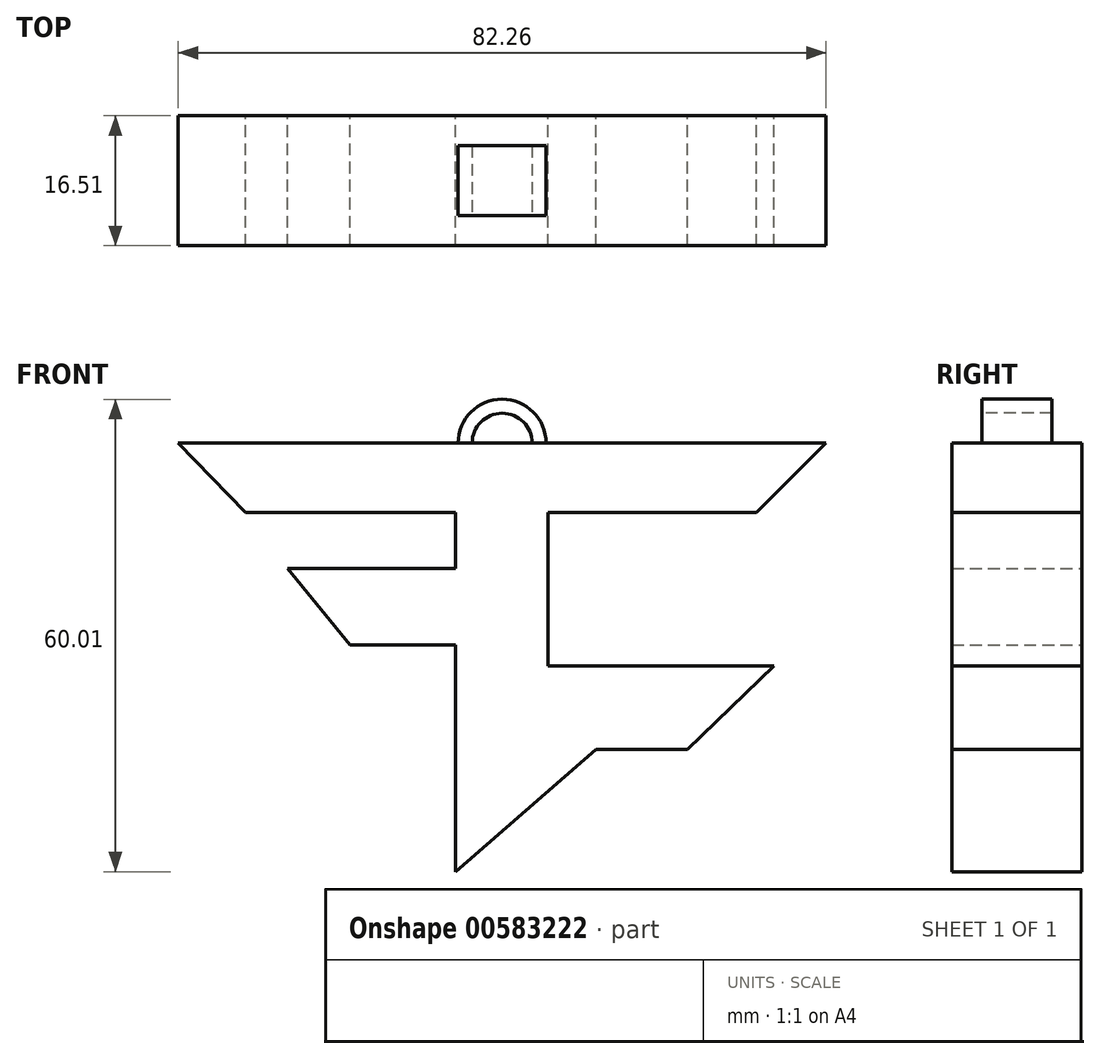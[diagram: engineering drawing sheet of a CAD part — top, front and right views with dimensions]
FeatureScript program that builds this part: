
annotation { "Feature Type Name" : "Feature", "Feature Type Description" : "" }
export const myFeature = defineFeature(function(context is Context, id is Id, definition is map)
    precondition{}
    {
        {
            var Q0;
            Q0=qCreatedBy(makeId("Front.planeOp"),FACE);
            var sketch = newSketch(context, id + "F0", { "sketchPlane" : qUnion([Q0])});
            skLineSegment(sketch, "E0", {"start": v(-131.37, 102.72) * mm, "end": v(-49.1, 102.72) * mm});
            skLineSegment(sketch, "E1", {"start": v(-49.1, 102.72) * mm, "end": v(-57.96, 93.95) * mm});
            skLineSegment(sketch, "E2", {"start": v(-57.96, 93.95) * mm, "end": v(-84.39, 93.95) * mm});
            skLineSegment(sketch, "E3", {"start": v(-84.39, 93.95) * mm, "end": v(-84.39, 74.4) * mm});
            skLineSegment(sketch, "E4", {"start": v(-84.39, 74.4) * mm, "end": v(-55.7, 74.4) * mm});
            skLineSegment(sketch, "E5", {"start": v(-55.7, 74.4) * mm, "end": v(-66.72, 63.82) * mm});
            skLineSegment(sketch, "E6", {"start": v(-66.72, 63.82) * mm, "end": v(-78.31, 63.82) * mm});
            skLineSegment(sketch, "E7", {"start": v(-78.31, 63.82) * mm, "end": v(-96.14, 48.29) * mm});
            skLineSegment(sketch, "E8", {"start": v(-96.14, 48.29) * mm, "end": v(-96.14, 77.09) * mm});
            skLineSegment(sketch, "E9", {"start": v(-96.14, 77.09) * mm, "end": v(-109.57, 77.09) * mm});
            skLineSegment(sketch, "E10", {"start": v(-109.57, 77.09) * mm, "end": v(-117.51, 86.78) * mm});
            skLineSegment(sketch, "E11", {"start": v(-117.51, 86.78) * mm, "end": v(-96.14, 86.78) * mm});
            skLineSegment(sketch, "E12", {"start": v(-96.14, 86.78) * mm, "end": v(-96.14, 93.95) * mm});
            skLineSegment(sketch, "E13", {"start": v(-96.14, 93.95) * mm, "end": v(-122.84, 93.95) * mm});
            skLineSegment(sketch, "E14", {"start": v(-122.84, 93.95) * mm, "end": v(-131.37, 102.72) * mm});
            skSolve(sketch);
        }
        {
            var Q0;
            Q0=makeQuery(id+"F0.imprint","IMPRINT",FACE,{"disambiguationData":[TD([[makeQuery(id+"F0.imprint","IMPRINT",EDGE,{"derivedFrom":sQuery(id+"F0.wireOp",EDGE,"E0")}),-1.0]])]});
            extrude(context, id + "F1", {"entities" : qUnion([Q0]), "depth" : 16.5 * mm, "offsetDistance" : 25.4 * mm});
        }
        {
            var Q0;
            Q0=makeQuery(id+"F1.opExtrude","CAP_FACE",FACE,{"disambiguationData":[OSD([sQuery(id+"F0.wireOp",EDGE,"E0"),sQuery(id+"F0.wireOp",EDGE,"E1"),sQuery(id+"F0.wireOp",EDGE,"E2"),sQuery(id+"F0.wireOp",EDGE,"E3"),sQuery(id+"F0.wireOp",EDGE,"E4"),sQuery(id+"F0.wireOp",EDGE,"E5"),sQuery(id+"F0.wireOp",EDGE,"E6"),sQuery(id+"F0.wireOp",EDGE,"E7"),sQuery(id+"F0.wireOp",EDGE,"E8"),sQuery(id+"F0.wireOp",EDGE,"E9"),sQuery(id+"F0.wireOp",EDGE,"E10"),sQuery(id+"F0.wireOp",EDGE,"E11"),sQuery(id+"F0.wireOp",EDGE,"E12"),sQuery(id+"F0.wireOp",EDGE,"E13"),sQuery(id+"F0.wireOp",EDGE,"E14")])],"isStart":false});
            var sketch = newSketch(context, id + "F2", { "sketchPlane" : qUnion([Q0])});
            skArc(sketch, "E15", {"start": v(-86.43, 102.72) * mm, "mid": v(-90.24, 106.53) * mm, "end": v(-94.05, 102.72) * mm});
            skArc(sketch, "E16", {"start": v(-84.65, 102.72) * mm, "mid": v(-90.24, 108.3) * mm, "end": v(-95.83, 102.72) * mm});
            skSolve(sketch);
        }
        {
            var Q0;
            {var subQ0=sQuery(id+"F2.wireOp",EDGE,"E15");Q0=makeQuery(id+"F2.imprint","IMPRINT",FACE,{"disambiguationData":[TD([[makeQuery(id+"F2.imprint","IMPRINT",EDGE,{"derivedFrom":subQ0}),-1.0]])]});}
            extrude(context, id + "F3", {"entities" : qUnion([Q0]), "operationType" : NewBodyOperationType.ADD, "oppositeDirection" : true, "depth" : 12.7 * mm, "offsetDistance" : 25.4 * mm});
        }
        {
            var Q0;
            {var subQ0=sQuery(id+"F0.wireOp",EDGE,"E0");Q0=makeQuery(id+"F3.boolean.opBoolean","MERGE",FACE,{"derivedFrom":[makeQuery(id+"F1.opExtrude","CAP_FACE",FACE,{"disambiguationData":[OSD([subQ0,sQuery(id+"F0.wireOp",EDGE,"E1"),sQuery(id+"F0.wireOp",EDGE,"E2"),sQuery(id+"F0.wireOp",EDGE,"E3"),sQuery(id+"F0.wireOp",EDGE,"E4"),sQuery(id+"F0.wireOp",EDGE,"E5"),sQuery(id+"F0.wireOp",EDGE,"E6"),sQuery(id+"F0.wireOp",EDGE,"E7"),sQuery(id+"F0.wireOp",EDGE,"E8"),sQuery(id+"F0.wireOp",EDGE,"E9"),sQuery(id+"F0.wireOp",EDGE,"E10"),sQuery(id+"F0.wireOp",EDGE,"E11"),sQuery(id+"F0.wireOp",EDGE,"E12"),sQuery(id+"F0.wireOp",EDGE,"E13"),sQuery(id+"F0.wireOp",EDGE,"E14")])],"isStart":false}),makeQuery(id+"F3.opExtrude","CAP_FACE",FACE,{"disambiguationData":[OSD([subQ0,sQuery(id+"F2.wireOp",EDGE,"E15"),sQuery(id+"F2.wireOp",EDGE,"E16")])],"isStart":true})]});}
            var sketch = newSketch(context, id + "F4", { "sketchPlane" : qUnion([Q0])});
            skArc(sketch, "E17", {"start": v(-84.65, 102.72) * mm, "mid": v(-90.24, 108.3) * mm, "end": v(-95.83, 102.72) * mm});
            skArc(sketch, "E18", {"start": v(-86.43, 102.72) * mm, "mid": v(-90.24, 106.53) * mm, "end": v(-94.05, 102.72) * mm});
            skLineSegment(sketch, "E19", {"start": v(-95.83, 102.72) * mm, "end": v(-94.05, 102.72) * mm});
            skLineSegment(sketch, "E20", {"start": v(-86.43, 102.72) * mm, "end": v(-84.65, 102.72) * mm});
            skSolve(sketch);
        }
        {
            var Q0;
            Q0=makeQuery(id+"F4.imprint","IMPRINT",FACE,{"disambiguationData":[TD([[makeQuery(id+"F4.imprint","IMPRINT",EDGE,{"derivedFrom":sQuery(id+"F4.wireOp",EDGE,"E17")}),1.0]])]});
            extrude(context, id + "F5", {"entities" : qUnion([Q0]), "operationType" : NewBodyOperationType.REMOVE, "oppositeDirection" : true, "depth" : 3.8 * mm, "offsetDistance" : 25.4 * mm});
        }
    });
